# Revit family: Алсель_Коллектора_Стальные
name_source: partatom
category: Соединительные детали трубопроводов
revit_build: Autodesk Revit 2016 (Build: 20150714_1515(x64)
units: mm (PartAtom-declared; Revit-internal decimal feet)

## family parameters
Всегда вертикально = Нет
На основе рабочей плоскости = Да
Общий = Нет
При загрузке вырезать с полостями = Нет
Размер круглого соединителя = Использовать диаметр
Тип детали = Мультипорт

## types (1)
- Алсель_Коллектора_Стальные
    ADSK_URL страницы изделия = http://www.ahlsell.ru
    ADSK_Диаметр условный = 50 мм
    ADSK_Единица измерения = шт.
    ADSK_Завод-изготовитель = Алсель
    ADSK_Код изделия = AHL50х34-5вых
    ADSK_Наименование = Коллектор стальной Ду50х3/4 нр+5 вых 1/2 нр
    ADSK_Страна производства = AHLSELL_PEX – Испания, Китай
    B_Патрубки = 50 мм
    C_Шаг_Выходов = 100 мм
    D_Диаметр_Коллектора = 60 мм
    F_DY_БоковыхПатрубков = 15 мм
    F_Диаметр_Коннектора = 15 мм
    G'_Диаметр_Выходов = 15 мм
    G_Диаметр_Входа = 20 мм
    L2_L1 = 110 мм
    L2_ДлинаОголовка = 50 мм
    L_Длина_Коллектора = 710 мм
    L_ДлинаРезьбы = 15 мм
    Выход_10 = 0 мм
    Выход_11 = 0 мм
    Выход_12 = 0 мм
    Выход_13 = 0 мм
    Выход_2 = 100 мм
    Выход_3 = 200 мм
    Выход_4 = 300 мм
    Выход_5 = 400 мм
    Выход_6 = 0 мм
    Выход_7 = 0 мм
    Выход_8 = 0 мм
    Выход_9 = 0 мм
    Длина_Выходов = 65 мм
    ДлинаБоковыхПатрубков = 58 мм
    Количество_Выходов = 5
    Отметка по умолчанию = 1500 мм
